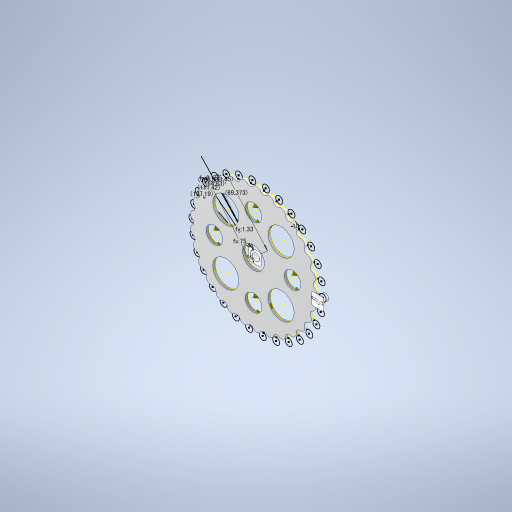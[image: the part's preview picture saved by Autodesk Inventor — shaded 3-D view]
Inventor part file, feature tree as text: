
AUTODESK INVENTOR PART (.ipt)
format: ipt  version: 2024 (Build 280153000, 153)  size: 681,472 bytes
history: native  units: mm
features: other x4, sketch x2, extrude x1, projected_geometry x1
ambient origin geometry x8: Origin, YZ Plane, XZ Plane, XY Plane, X Axis, Y Axis, Z Axis, Center Point
bodies: Body1 (feature_tree)
feature tree (8):
  other  "サイクロイドギア.ipt"
  extrude  "押し出し1"  Depth=10.0mm
  sketch  "スケッチ2"
  other  "ソリッド1::サイクロイドギア.ipt"
  other  "TaggingFeature1"
  sketch  "スケッチ1"
  projected_geometry  "投影ループ1"
  other  "ソリッド1"
